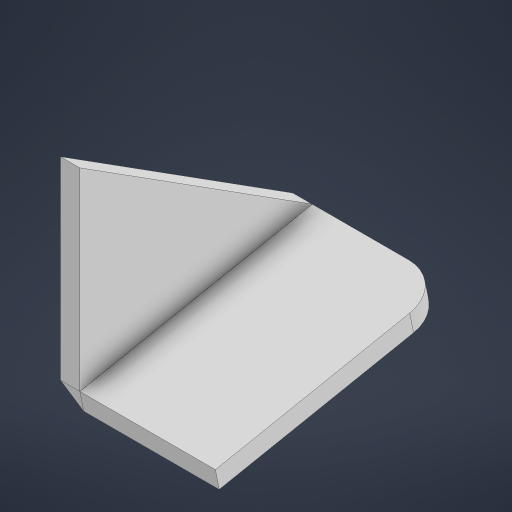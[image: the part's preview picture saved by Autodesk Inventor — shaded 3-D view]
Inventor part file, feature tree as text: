
AUTODESK INVENTOR PART (.ipt)
format: ipt  version: 2023 (Build 270158000, 158)  size: 200,704 bytes
history: native  units: in
note: dims shown in document units (in); Inventor stores cm internally (conversion verified against a paired STEP export)
features: extrude x2, sketch x2, other x2, loft x1, fillet x1
ambient origin geometry x8: Origin, YZ Plane, XZ Plane, XY Plane, X Axis, Y Axis, Z Axis, Center Point
bodies: Solid1 (feature_tree), Solid2 (feature_tree)
feature tree (8):
  extrude  "Extrusion1"  Depth=0.5in TaperAngle=0.0deg
  extrude  "Extrusion2"  Depth=1.0in
  loft  "Loft1"
  fillet  "Fillet1"  [1 undecoded]
  sketch  "Sketch1"  dims[d0=5.0in d2=0.5in d3=0.0in]
  sketch  "Sketch2"  dims[d5=0.077in d6=6.0in d7=0.0in d8=0.0in d9=3.5in d10=0.5in d11=0.0in d12=0.0in d13=90.0deg d14=0.0in d15=90.0deg d16=1.0in]
  other  "Edges1"
  other  "Edges2"
note: 1 required parameter value undecoded (feature->parameter linkage not recoverable at this tier; creation-order binding heuristic only, values carry confidence <= 0.55)
